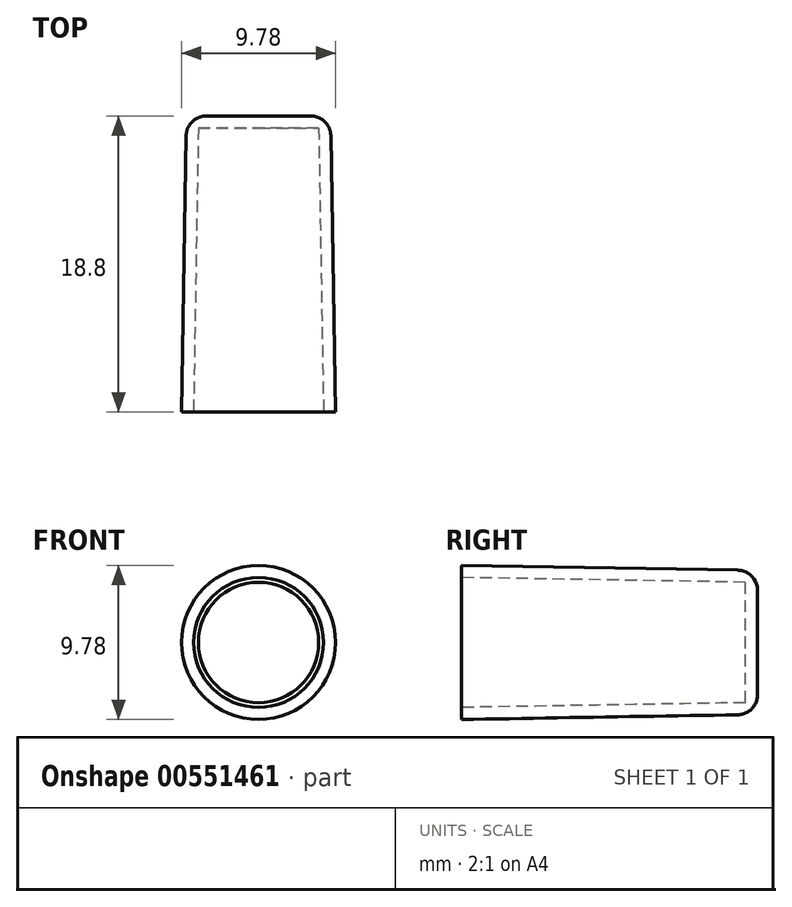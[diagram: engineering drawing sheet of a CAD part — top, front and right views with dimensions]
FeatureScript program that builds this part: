
annotation { "Feature Type Name" : "Feature", "Feature Type Description" : "" }
export const myFeature = defineFeature(function(context is Context, id is Id, definition is map)
    precondition{}
    {
        {
            var Q0;
            Q0=qCreatedBy(makeId("Front.planeOp"),FACE);
            var sketch = newSketch(context, id + "F0", { "sketchPlane" : qUnion([Q0])});
            skCircle(sketch, "E0", {"center": v(0, 0) * mm, "radius": 4.57 * mm});
            skSolve(sketch);
        }
        {
            var Q0;
            Q0=qCreatedBy(makeId("Front.planeOp"),FACE);
            cPlane(context, id + "F1", {"entities" : qUnion([Q0]), "cplaneType" : CPlaneType.OFFSET, "offset" : 18.8 * mm, "width" : 152.4 * mm, "height" : 152.4 * mm});
        }
        {
            var Q0;
            Q0=qCreatedBy(id+"F1.planeOp",FACE);
            var sketch = newSketch(context, id + "F2", { "sketchPlane" : qUnion([Q0])});
            skCircle(sketch, "E1", {"center": v(0, 0) * mm, "radius": 4.89 * mm});
            skSolve(sketch);
        }
        {
            var Q0;
            Q0=makeQuery(id+"F0.imprint","IMPRINT",FACE,{"disambiguationData":[TD([[makeQuery(id+"F0.imprint","IMPRINT",EDGE,{"derivedFrom":sQuery(id+"F0.wireOp",EDGE,"E0")}),1.0]])]});
            var Q1;
            Q1=makeQuery(id+"F2.imprint","IMPRINT",FACE,{"disambiguationData":[TD([[makeQuery(id+"F2.imprint","IMPRINT",EDGE,{"derivedFrom":sQuery(id+"F2.wireOp",EDGE,"E1")}),1.0]])]});
            loft(context, id + "F3", {"sheetProfilesArray" : [{ "sheetProfileEntities" : qUnion([Q0]) }, { "sheetProfileEntities" : qUnion([Q1]) }]});
        }
        {
            var Q0;
            Q0=makeQuery(id+"F3.opLoft","CAP_FACE",FACE,{"disambiguationData":[OSD([makeQuery(id+"F2.imprint","IMPRINT",FACE,{"disambiguationData":[TD([[makeQuery(id+"F2.imprint","IMPRINT",EDGE,{"derivedFrom":sQuery(id+"F2.wireOp",EDGE,"E1")}),1.0]])]})])],"isStart":true});
            shell(context, id + "F4", {"entities" : qUnion([Q0]), "thickness" : 0.76 * mm});
        }
        {
            var Q0;
            Q0=makeQuery(id+"F3.opLoft","MID_CAP_EDGE",EDGE,{"disambiguationData":[OSD([sQuery(id+"F0.wireOp",EDGE,"E0")])],"capPos":0.0});
            fillet(context, id + "F5", {"entities" : qUnion([Q0]), "radius" : 1.27 * mm, "tangentPropagation" : true, "allowEdgeOverflow" : false});
        }
    });
